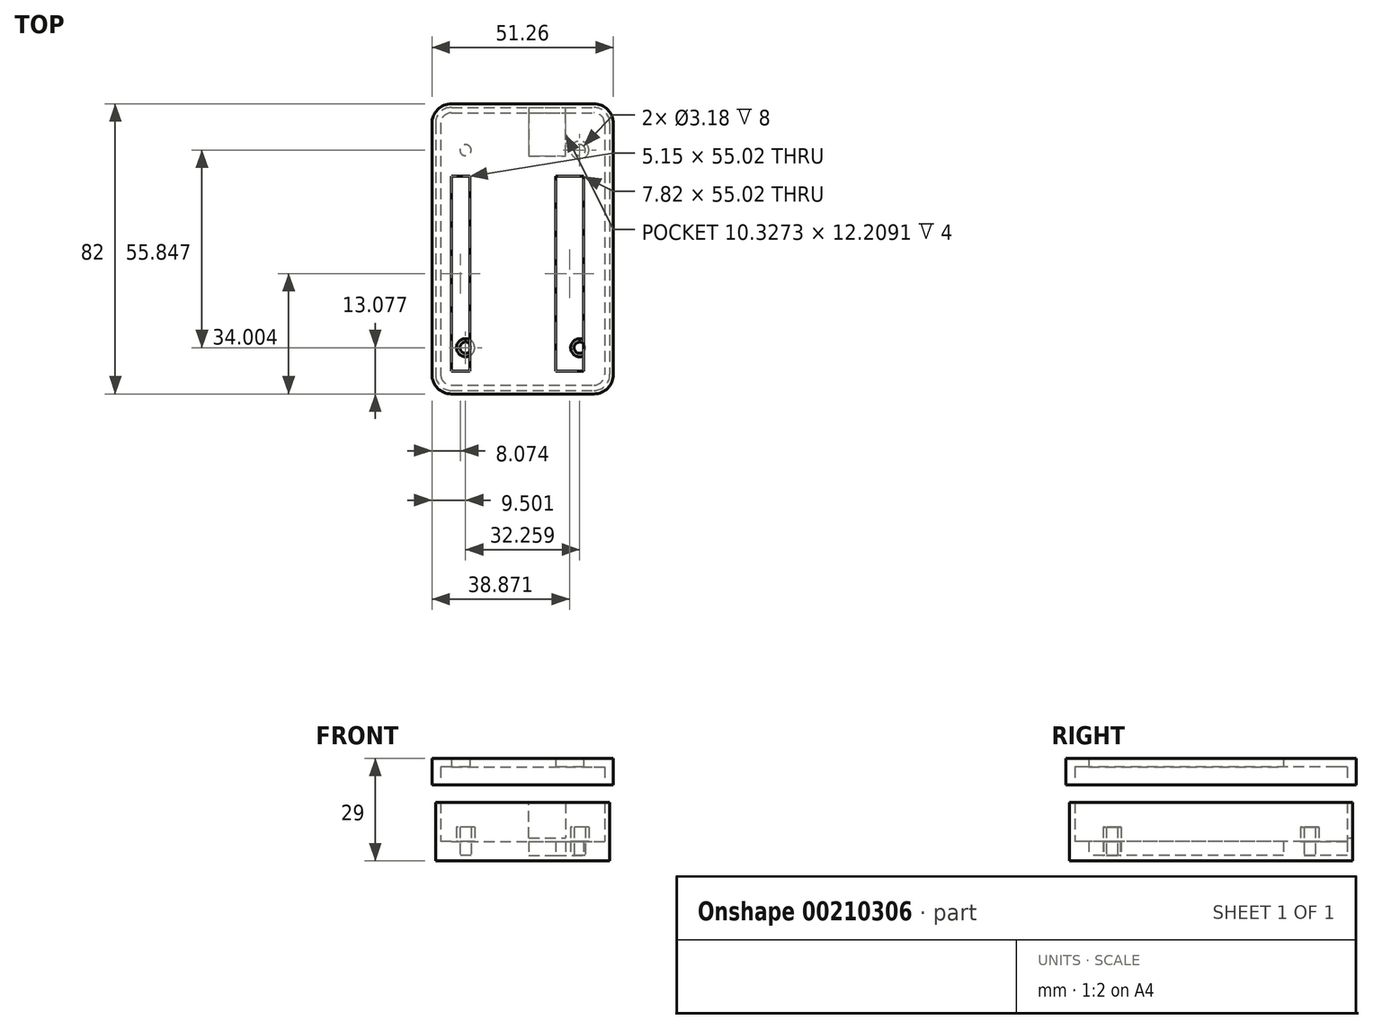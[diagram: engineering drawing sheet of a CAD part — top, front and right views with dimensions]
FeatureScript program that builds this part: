
annotation { "Feature Type Name" : "Feature", "Feature Type Description" : "" }
export const myFeature = defineFeature(function(context is Context, id is Id, definition is map)
    precondition{}
    {
        {
            var Q0;
            Q0=qCreatedBy(makeId("Top.planeOp"),FACE);
            var sketch = newSketch(context, id + "F0", { "sketchPlane" : qUnion([Q0])});
            skLineSegment(sketch, "E0.bottom", {"start": v(-20.13, 38.5) * mm, "end": v(20.13, 38.5) * mm});
            skLineSegment(sketch, "E0.top", {"start": v(-20.13, -38.5) * mm, "end": v(20.13, -38.5) * mm});
            skLineSegment(sketch, "E0.left", {"start": v(-23.13, 35.5) * mm, "end": v(-23.13, -35.5) * mm});
            skLineSegment(sketch, "E0.right", {"start": v(23.13, 35.5) * mm, "end": v(23.13, -35.5) * mm});
            skPoint(sketch, "E1.visualSharp", {"position": v(-23.13, 38.5) * mm});
            skArc(sketch, "E1.filletArc", {"start": v(-20.13, 38.5) * mm, "mid": v(-22.25, 37.62) * mm, "end": v(-23.13, 35.5) * mm});
            skPoint(sketch, "E2.visualSharp", {"position": v(23.13, 38.5) * mm});
            skArc(sketch, "E2.filletArc", {"start": v(23.13, 35.5) * mm, "mid": v(22.25, 37.62) * mm, "end": v(20.13, 38.5) * mm});
            skPoint(sketch, "E3.visualSharp", {"position": v(23.13, -38.5) * mm});
            skArc(sketch, "E3.filletArc", {"start": v(20.13, -38.5) * mm, "mid": v(22.25, -37.62) * mm, "end": v(23.13, -35.5) * mm});
            skPoint(sketch, "E4.visualSharp", {"position": v(-23.13, -38.5) * mm});
            skArc(sketch, "E4.filletArc", {"start": v(-23.13, -35.5) * mm, "mid": v(-22.25, -37.62) * mm, "end": v(-20.13, -38.5) * mm});
            skLineSegment(sketch, "E5", {"start": v(1.76, 38.5) * mm, "end": v(1.76, 26.3) * mm});
            skLineSegment(sketch, "E6", {"start": v(1.76, 26.3) * mm, "end": v(12.08, 26.3) * mm});
            skLineSegment(sketch, "E7", {"start": v(12.08, 26.3) * mm, "end": v(12.08, 38.5) * mm});
            skLineSegment(sketch, "E8.bottom", {"start": v(-20.13, 20.51) * mm, "end": v(-14.98, 20.51) * mm});
            skLineSegment(sketch, "E8.top", {"start": v(-20.13, -34.5) * mm, "end": v(-14.98, -34.5) * mm});
            skLineSegment(sketch, "E8.left", {"start": v(-20.13, 20.51) * mm, "end": v(-20.13, -34.5) * mm});
            skLineSegment(sketch, "E8.right", {"start": v(-14.98, 20.51) * mm, "end": v(-14.98, -34.5) * mm});
            skLineSegment(sketch, "E9.bottom", {"start": v(9.33, 20.51) * mm, "end": v(17.15, 20.51) * mm});
            skLineSegment(sketch, "E9.top", {"start": v(9.33, -34.5) * mm, "end": v(17.15, -34.5) * mm});
            skLineSegment(sketch, "E9.left", {"start": v(9.33, 20.51) * mm, "end": v(9.33, -34.5) * mm});
            skLineSegment(sketch, "E9.right", {"start": v(17.15, 20.51) * mm, "end": v(17.15, -34.5) * mm});
            skLineSegment(sketch, "E10", {"start": v(-14.98, 20.51) * mm, "end": v(9.33, 20.51) * mm, "construction": true});
            skLineSegment(sketch, "E11", {"start": v(-14.98, -34.5) * mm, "end": v(9.33, -34.5) * mm, "construction": true});
            skLineSegment(sketch, "E12", {"start": v(1.76, 38.5) * mm, "end": v(1.76, 43.07) * mm});
            skLineSegment(sketch, "E13", {"start": v(1.76, 43.07) * mm, "end": v(12.08, 43.07) * mm});
            skLineSegment(sketch, "E14", {"start": v(12.08, 43.07) * mm, "end": v(12.08, 38.5) * mm});
            skLineSegment(sketch, "E15", {"start": v(0, 0) * mm, "end": v(-23.13, 0) * mm, "construction": true});
            skLineSegment(sketch, "E16", {"start": v(0, 0) * mm, "end": v(0, -38.5) * mm, "construction": true});
            skSolve(sketch);
        }
        {
            var Q0;
            Q0=makeQuery(id+"F0.imprint","IMPRINT",FACE,{"disambiguationData":[TD([[makeQuery(id+"F0.imprint","IMPRINT",EDGE,{"derivedFrom":sQuery(id+"F0.wireOp",EDGE,"E0.top")}),1.0]])]});
            var Q1;
            {var subQ0=sQuery(id+"F0.wireOp",EDGE,"E5");Q1=makeQuery(id+"F0.imprint","IMPRINT",FACE,{"disambiguationData":[TD([[makeQuery(id+"F0.imprint","IMPRINT",EDGE,{"derivedFrom":subQ0}),1.0]])]});}
            var Q2;
            Q2=makeQuery(id+"F0.imprint","IMPRINT",FACE,{"disambiguationData":[TD([[makeQuery(id+"F0.imprint","IMPRINT",EDGE,{"derivedFrom":sQuery(id+"F0.wireOp",EDGE,"E9.bottom")}),-1.0]])]});
            var Q3;
            Q3=makeQuery(id+"F0.imprint","IMPRINT",FACE,{"disambiguationData":[TD([[makeQuery(id+"F0.imprint","IMPRINT",EDGE,{"derivedFrom":sQuery(id+"F0.wireOp",EDGE,"E8.bottom")}),-1.0]])]});
            extrude(context, id + "F1", {"entities" : qUnion([Q0, Q1, Q2, Q3]), "depth" : 15 * mm});
        }
        {
            var Q0;
            Q0=makeQuery(id+"F1.opExtrude","CAP_FACE",FACE,{"disambiguationData":[OSD([sQuery(id+"F0.wireOp",EDGE,"E0.bottom"),sQuery(id+"F0.wireOp",EDGE,"E0.top"),sQuery(id+"F0.wireOp",EDGE,"E0.left"),sQuery(id+"F0.wireOp",EDGE,"E0.right"),sQuery(id+"F0.wireOp",EDGE,"E1.filletArc"),sQuery(id+"F0.wireOp",EDGE,"E2.filletArc"),sQuery(id+"F0.wireOp",EDGE,"E3.filletArc"),sQuery(id+"F0.wireOp",EDGE,"E4.filletArc")])],"isStart":false});
            shell(context, id + "F2", {"entities" : qUnion([Q0]), "thickness" : 1.5 * mm, "oppositeDirection" : true});
        }
        {
            var Q0;
            {var subQ0=sQuery(id+"F0.wireOp",EDGE,"E12");Q0=makeQuery(id+"F0.imprint","IMPRINT",FACE,{"disambiguationData":[TD([[makeQuery(id+"F0.imprint","IMPRINT",EDGE,{"derivedFrom":subQ0}),-1.0]])]});}
            var Q1;
            {var subQ0=sQuery(id+"F0.wireOp",EDGE,"E5");Q1=makeQuery(id+"F0.imprint","IMPRINT",FACE,{"disambiguationData":[TD([[makeQuery(id+"F0.imprint","IMPRINT",EDGE,{"derivedFrom":subQ0}),1.0]])]});}
            extrude(context, id + "F3", {"entities" : qUnion([Q0, Q1]), "operationType" : NewBodyOperationType.REMOVE, "depth" : 20 * mm, "hasSecondDirection" : true, "secondDirectionOppositeDirection" : false, "secondDirectionDepth" : 5 * mm});
        }
        {
            var Q0;
            Q0=makeQuery(id+"F0.imprint","IMPRINT",FACE,{"disambiguationData":[TD([[makeQuery(id+"F0.imprint","IMPRINT",EDGE,{"derivedFrom":sQuery(id+"F0.wireOp",EDGE,"E0.top")}),1.0]])]});
            var Q1;
            {var subQ0=sQuery(id+"F0.wireOp",EDGE,"E5");Q1=makeQuery(id+"F0.imprint","IMPRINT",FACE,{"disambiguationData":[TD([[makeQuery(id+"F0.imprint","IMPRINT",EDGE,{"derivedFrom":subQ0}),1.0]])]});}
            var Q2;
            Q2=makeQuery(id+"F0.imprint","IMPRINT",FACE,{"disambiguationData":[TD([[makeQuery(id+"F0.imprint","IMPRINT",EDGE,{"derivedFrom":sQuery(id+"F0.wireOp",EDGE,"E8.bottom")}),-1.0]])]});
            var Q3;
            Q3=makeQuery(id+"F0.imprint","IMPRINT",FACE,{"disambiguationData":[TD([[makeQuery(id+"F0.imprint","IMPRINT",EDGE,{"derivedFrom":sQuery(id+"F0.wireOp",EDGE,"E9.bottom")}),-1.0]])]});
            extrude(context, id + "F4", {"entities" : qUnion([Q0, Q1, Q2, Q3]), "depth" : 25 * mm, "hasSecondDirection" : true, "secondDirectionOppositeDirection" : false, "secondDirectionDepth" : 20 * mm});
        }
        {
            var Q0;
            Q0=makeQuery(id+"F4.opExtrude","CAP_FACE",FACE,{"disambiguationData":[OSD([sQuery(id+"F0.wireOp",EDGE,"E0.bottom"),sQuery(id+"F0.wireOp",EDGE,"E0.top"),sQuery(id+"F0.wireOp",EDGE,"E0.left"),sQuery(id+"F0.wireOp",EDGE,"E0.right"),sQuery(id+"F0.wireOp",EDGE,"E1.filletArc"),sQuery(id+"F0.wireOp",EDGE,"E2.filletArc"),sQuery(id+"F0.wireOp",EDGE,"E3.filletArc"),sQuery(id+"F0.wireOp",EDGE,"E4.filletArc")])],"isStart":true});
            shell(context, id + "F5", {"entities" : qUnion([Q0]), "thickness" : 2.5 * mm, "oppositeDirection" : true});
        }
        {
            var Q0;
            Q0=makeQuery(id+"F0.imprint","IMPRINT",FACE,{"disambiguationData":[TD([[makeQuery(id+"F0.imprint","IMPRINT",EDGE,{"derivedFrom":sQuery(id+"F0.wireOp",EDGE,"E8.bottom")}),-1.0]])]});
            var Q1;
            Q1=makeQuery(id+"F0.imprint","IMPRINT",FACE,{"disambiguationData":[TD([[makeQuery(id+"F0.imprint","IMPRINT",EDGE,{"derivedFrom":sQuery(id+"F0.wireOp",EDGE,"E9.bottom")}),-1.0]])]});
            extrude(context, id + "F6", {"entities" : qUnion([Q0, Q1]), "operationType" : NewBodyOperationType.REMOVE, "depth" : 33.1 * mm});
        }
        {
            var Q0;
            Q0=makeQuery(id+"F0.imprint","IMPRINT",FACE,{"disambiguationData":[TD([[makeQuery(id+"F0.imprint","IMPRINT",EDGE,{"derivedFrom":sQuery(id+"F0.wireOp",EDGE,"E0.top")}),1.0]])]});
            var sketch = newSketch(context, id + "F7", { "sketchPlane" : qUnion([Q0])});
            skLineSegment(sketch, "E17.0", {"start": v(-23.13, 35.5) * mm, "end": v(-23.13, -35.5) * mm});
            skLineSegment(sketch, "E18.0", {"start": v(-20.13, -38.5) * mm, "end": v(20.13, -38.5) * mm});
            skLineSegment(sketch, "E19.0", {"start": v(-20.13, 38.5) * mm, "end": v(20.13, 38.5) * mm});
            skLineSegment(sketch, "E20.0", {"start": v(23.13, 35.5) * mm, "end": v(23.13, -35.5) * mm});
            skCircle(sketch, "E21", {"center": v(-16.13, 27.92) * mm, "radius": 2.56 * mm});
            skLineSegment(sketch, "E22", {"start": v(0, 0) * mm, "end": v(0, 24.9) * mm});
            skLineSegment(sketch, "E23", {"start": v(0, 0) * mm, "end": v(-16.33, 0) * mm});
            skCircle(sketch, "E24", {"center": v(-16.13, 27.92) * mm, "radius": 1.59 * mm});
            skCircle(sketch, "E25.MirrorC", {"center": v(16.13, 27.92) * mm, "radius": 2.56 * mm});
            skCircle(sketch, "E26.MirrorC", {"center": v(16.13, 27.92) * mm, "radius": 1.59 * mm});
            skCircle(sketch, "E27.MirrorC", {"center": v(-16.13, -27.92) * mm, "radius": 2.56 * mm});
            skCircle(sketch, "E28.MirrorC", {"center": v(-16.13, -27.92) * mm, "radius": 1.59 * mm});
            skCircle(sketch, "E29.MirrorC", {"center": v(16.13, -27.92) * mm, "radius": 1.59 * mm});
            skCircle(sketch, "E30.MirrorC", {"center": v(16.13, -27.92) * mm, "radius": 2.56 * mm});
            skSolve(sketch);
        }
        {
            var Q0;
            Q0=makeQuery(id+"F7.imprint","IMPRINT",FACE,{"disambiguationData":[TD([[makeQuery(id+"F7.imprint","IMPRINT",EDGE,{"derivedFrom":sQuery(id+"F7.wireOp",EDGE,"E24")}),1.0]])]});
            var Q1;
            Q1=makeQuery(id+"F7.imprint","IMPRINT",FACE,{"disambiguationData":[TD([[makeQuery(id+"F7.imprint","IMPRINT",EDGE,{"derivedFrom":sQuery(id+"F7.wireOp",EDGE,"E26.MirrorC")}),-1.0]])]});
            var Q2;
            {var subQ0=sQuery(id+"F7.wireOp",EDGE,"E28.MirrorC");var subQ1=makeQuery(id+"F0.imprint","IMPRINT",EDGE,{"derivedFrom":sQuery(id+"F0.wireOp",EDGE,"E8.right")});var subQ2=makeQuery(id+"F7.imprint","INTERSECT",VERTEX,{"disambiguationData":[OD(0.0)],"derivedFrom":[subQ1,subQ0]});Q2=makeQuery(id+"F7.imprint","IMPRINT",FACE,{"disambiguationData":[TD([[makeQuery(id+"F7.imprint","IMPRINT",EDGE,{"disambiguationData":[TD([[subQ2,-1.0]])],"derivedFrom":subQ0}),-1.0]])]});}
            var Q3;
            {var subQ0=sQuery(id+"F7.wireOp",EDGE,"E28.MirrorC");var subQ1=makeQuery(id+"F0.imprint","IMPRINT",EDGE,{"derivedFrom":sQuery(id+"F0.wireOp",EDGE,"E8.right")});var subQ2=makeQuery(id+"F7.imprint","INTERSECT",VERTEX,{"disambiguationData":[OD(0.0)],"derivedFrom":[subQ1,subQ0]});Q3=makeQuery(id+"F7.imprint","IMPRINT",FACE,{"disambiguationData":[TD([[makeQuery(id+"F7.imprint","IMPRINT",EDGE,{"disambiguationData":[TD([[subQ2,1.0]])],"derivedFrom":subQ0}),-1.0]])]});}
            var Q4;
            {var subQ0=sQuery(id+"F7.wireOp",EDGE,"E29.MirrorC");var subQ1=makeQuery(id+"F0.imprint","IMPRINT",EDGE,{"derivedFrom":sQuery(id+"F0.wireOp",EDGE,"E9.right")});var subQ2=makeQuery(id+"F7.imprint","INTERSECT",VERTEX,{"disambiguationData":[OD(0.0)],"derivedFrom":[subQ1,subQ0]});Q4=makeQuery(id+"F7.imprint","IMPRINT",FACE,{"disambiguationData":[TD([[makeQuery(id+"F7.imprint","IMPRINT",EDGE,{"disambiguationData":[TD([[subQ2,-1.0]])],"derivedFrom":subQ0}),1.0]])]});}
            var Q5;
            {var subQ0=sQuery(id+"F7.wireOp",EDGE,"E29.MirrorC");var subQ1=makeQuery(id+"F0.imprint","IMPRINT",EDGE,{"derivedFrom":sQuery(id+"F0.wireOp",EDGE,"E9.right")});var subQ2=makeQuery(id+"F7.imprint","INTERSECT",VERTEX,{"disambiguationData":[OD(0.0)],"derivedFrom":[subQ1,subQ0]});Q5=makeQuery(id+"F7.imprint","IMPRINT",FACE,{"disambiguationData":[TD([[makeQuery(id+"F7.imprint","IMPRINT",EDGE,{"disambiguationData":[TD([[subQ2,1.0]])],"derivedFrom":subQ0}),1.0]])]});}
            extrude(context, id + "F8", {"entities" : qUnion([Q0, Q1, Q2, Q3, Q4, Q5]), "operationType" : NewBodyOperationType.ADD, "depth" : 8 * mm});
        }
        {
            var Q0;
            Q0=makeQuery(id+"F7.imprint","IMPRINT",FACE,{"disambiguationData":[TD([[makeQuery(id+"F7.imprint","IMPRINT",EDGE,{"derivedFrom":sQuery(id+"F7.wireOp",EDGE,"E21")}),1.0]])]});
            var Q1;
            Q1=makeQuery(id+"F7.imprint","IMPRINT",FACE,{"disambiguationData":[TD([[makeQuery(id+"F7.imprint","IMPRINT",EDGE,{"derivedFrom":sQuery(id+"F7.wireOp",EDGE,"E25.MirrorC")}),-1.0]])]});
            var Q2;
            {var subQ0=sQuery(id+"F7.wireOp",EDGE,"E27.MirrorC");var subQ1=makeQuery(id+"F0.imprint","IMPRINT",EDGE,{"derivedFrom":sQuery(id+"F0.wireOp",EDGE,"E8.right")});var subQ2=makeQuery(id+"F7.imprint","INTERSECT",VERTEX,{"disambiguationData":[OD(0.0)],"derivedFrom":[subQ1,subQ0]});Q2=makeQuery(id+"F7.imprint","IMPRINT",FACE,{"disambiguationData":[TD([[makeQuery(id+"F7.imprint","IMPRINT",EDGE,{"disambiguationData":[TD([[subQ2,-1.0]])],"derivedFrom":subQ0}),-1.0]])]});}
            var Q3;
            {var subQ0=sQuery(id+"F7.wireOp",EDGE,"E27.MirrorC");var subQ1=makeQuery(id+"F0.imprint","IMPRINT",EDGE,{"derivedFrom":sQuery(id+"F0.wireOp",EDGE,"E8.right")});var subQ2=makeQuery(id+"F7.imprint","INTERSECT",VERTEX,{"disambiguationData":[OD(0.0)],"derivedFrom":[subQ1,subQ0]});Q3=makeQuery(id+"F7.imprint","IMPRINT",FACE,{"disambiguationData":[TD([[makeQuery(id+"F7.imprint","IMPRINT",EDGE,{"disambiguationData":[TD([[subQ2,1.0]])],"derivedFrom":subQ0}),-1.0]])]});}
            var Q4;
            {var subQ0=sQuery(id+"F7.wireOp",EDGE,"E29.MirrorC");var subQ1=makeQuery(id+"F0.imprint","IMPRINT",EDGE,{"derivedFrom":sQuery(id+"F0.wireOp",EDGE,"E9.right")});var subQ2=makeQuery(id+"F7.imprint","INTERSECT",VERTEX,{"disambiguationData":[OD(0.0)],"derivedFrom":[subQ1,subQ0]});Q4=makeQuery(id+"F7.imprint","IMPRINT",FACE,{"disambiguationData":[TD([[makeQuery(id+"F7.imprint","IMPRINT",EDGE,{"disambiguationData":[TD([[subQ2,-1.0]])],"derivedFrom":subQ0}),-1.0]])]});}
            var Q5;
            {var subQ0=sQuery(id+"F7.wireOp",EDGE,"E29.MirrorC");var subQ1=makeQuery(id+"F0.imprint","IMPRINT",EDGE,{"derivedFrom":sQuery(id+"F0.wireOp",EDGE,"E9.right")});var subQ2=makeQuery(id+"F7.imprint","INTERSECT",VERTEX,{"disambiguationData":[OD(0.0)],"derivedFrom":[subQ1,subQ0]});Q5=makeQuery(id+"F7.imprint","IMPRINT",FACE,{"disambiguationData":[TD([[makeQuery(id+"F7.imprint","IMPRINT",EDGE,{"disambiguationData":[TD([[subQ2,1.0]])],"derivedFrom":subQ0}),-1.0]])]});}
            extrude(context, id + "F9", {"entities" : qUnion([Q0, Q1, Q2, Q3, Q4, Q5]), "operationType" : NewBodyOperationType.ADD, "depth" : 4 * mm});
        }
    });
